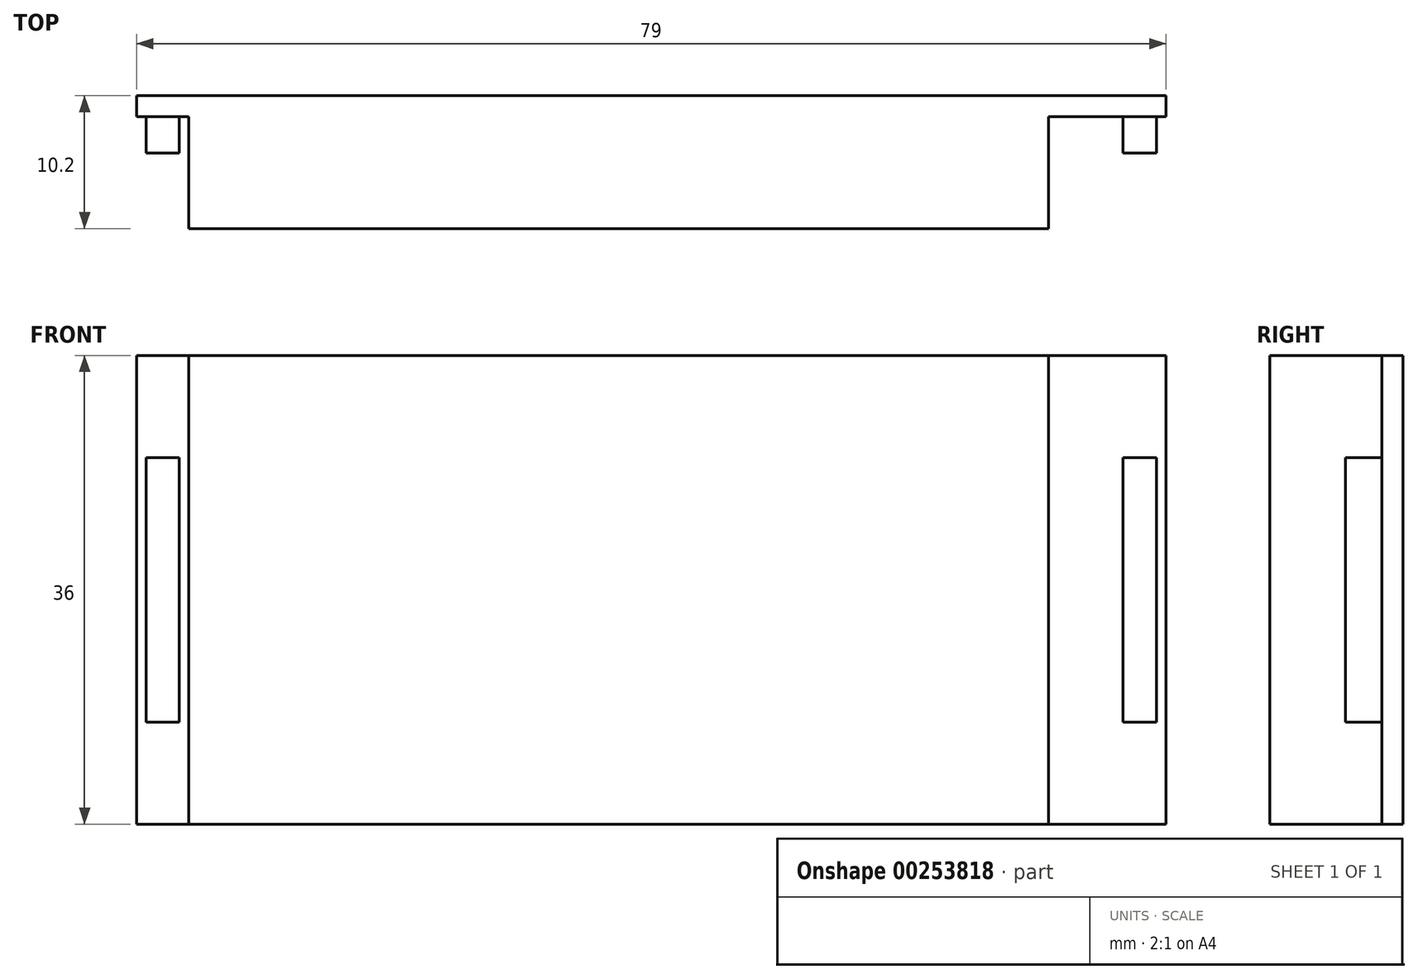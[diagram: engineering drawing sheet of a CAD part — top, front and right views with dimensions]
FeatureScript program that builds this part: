
annotation { "Feature Type Name" : "Feature", "Feature Type Description" : "" }
export const myFeature = defineFeature(function(context is Context, id is Id, definition is map)
    precondition{}
    {
        {
            var Q0;
            Q0=qCreatedBy(makeId("Front.planeOp"),FACE);
            var sketch = newSketch(context, id + "F0", { "sketchPlane" : qUnion([Q0])});
            skLineSegment(sketch, "E0.bottom", {"start": v(39.5, -18) * mm, "end": v(-39.5, -18) * mm});
            skLineSegment(sketch, "E0.top", {"start": v(39.5, 18) * mm, "end": v(-39.5, 18) * mm});
            skLineSegment(sketch, "E0.left", {"start": v(39.5, -18) * mm, "end": v(39.5, 18) * mm});
            skLineSegment(sketch, "E0.right", {"start": v(-39.5, -18) * mm, "end": v(-39.5, 18) * mm});
            skPoint(sketch, "E0.middle", {"position": v(0, 0) * mm});
            skSolve(sketch);
        }
        {
            var Q0;
            Q0 = qSketchRegion(id + "F0", true);
            extrude(context, id + "F1", {"entities" : qUnion([Q0]), "depth" : 1.6 * mm});
        }
        {
            var Q0;
            Q0=makeQuery(id+"F1.opExtrude","CAP_FACE",FACE,{"disambiguationData":[OSD([sQuery(id+"F0.wireOp",EDGE,"E0.bottom"),sQuery(id+"F0.wireOp",EDGE,"E0.top"),sQuery(id+"F0.wireOp",EDGE,"E0.left"),sQuery(id+"F0.wireOp",EDGE,"E0.right")])],"isStart":false});
            var sketch = newSketch(context, id + "F2", { "sketchPlane" : qUnion([Q0])});
            skLineSegment(sketch, "E1.bottom", {"start": v(-35.5, 18) * mm, "end": v(30.5, 18) * mm});
            skLineSegment(sketch, "E1.top", {"start": v(-35.5, -18) * mm, "end": v(30.5, -18) * mm});
            skLineSegment(sketch, "E1.left", {"start": v(-35.5, 18) * mm, "end": v(-35.5, -18) * mm});
            skLineSegment(sketch, "E1.right", {"start": v(30.5, 18) * mm, "end": v(30.5, -18) * mm});
            skSolve(sketch);
        }
        {
            var Q0;
            Q0 = qSketchRegion(id + "F2", true);
            extrude(context, id + "F3", {"entities" : qUnion([Q0]), "operationType" : NewBodyOperationType.ADD, "depth" : 8.6 * mm});
        }
        {
            var Q0;
            {var subQ0=sQuery(id+"F2.wireOp",EDGE,"E1.left");Q0=makeQuery(id+"F2.imprint","IMPRINT",FACE,{"disambiguationData":[TD([[makeQuery(id+"F2.imprint","IMPRINT",EDGE,{"derivedFrom":subQ0}),-1.0]])]});}
            var sketch = newSketch(context, id + "F4", { "sketchPlane" : qUnion([Q0])});
            skPoint(sketch, "E2", {"position": v(-37.5, 0) * mm});
            skPoint(sketch, "E3", {"position": v(37.5, 0) * mm});
            skLineSegment(sketch, "E4.bottom", {"start": v(-36.23, -10.16) * mm, "end": v(-38.77, -10.16) * mm});
            skLineSegment(sketch, "E4.top", {"start": v(-36.23, 10.16) * mm, "end": v(-38.77, 10.16) * mm});
            skLineSegment(sketch, "E4.left", {"start": v(-36.23, -10.16) * mm, "end": v(-36.23, 10.16) * mm});
            skLineSegment(sketch, "E4.right", {"start": v(-38.77, -10.16) * mm, "end": v(-38.77, 10.16) * mm});
            skLineSegment(sketch, "E5.bottom", {"start": v(36.23, -10.16) * mm, "end": v(38.77, -10.16) * mm});
            skLineSegment(sketch, "E5.top", {"start": v(36.23, 10.16) * mm, "end": v(38.77, 10.16) * mm});
            skLineSegment(sketch, "E5.left", {"start": v(36.23, -10.16) * mm, "end": v(36.23, 10.16) * mm});
            skLineSegment(sketch, "E5.right", {"start": v(38.77, -10.16) * mm, "end": v(38.77, 10.16) * mm});
            skSolve(sketch);
        }
        {
            var Q0;
            Q0 = qSketchRegion(id + "F4", true);
            extrude(context, id + "F5", {"entities" : qUnion([Q0]), "operationType" : NewBodyOperationType.ADD, "depth" : 2.8 * mm});
        }
    });
